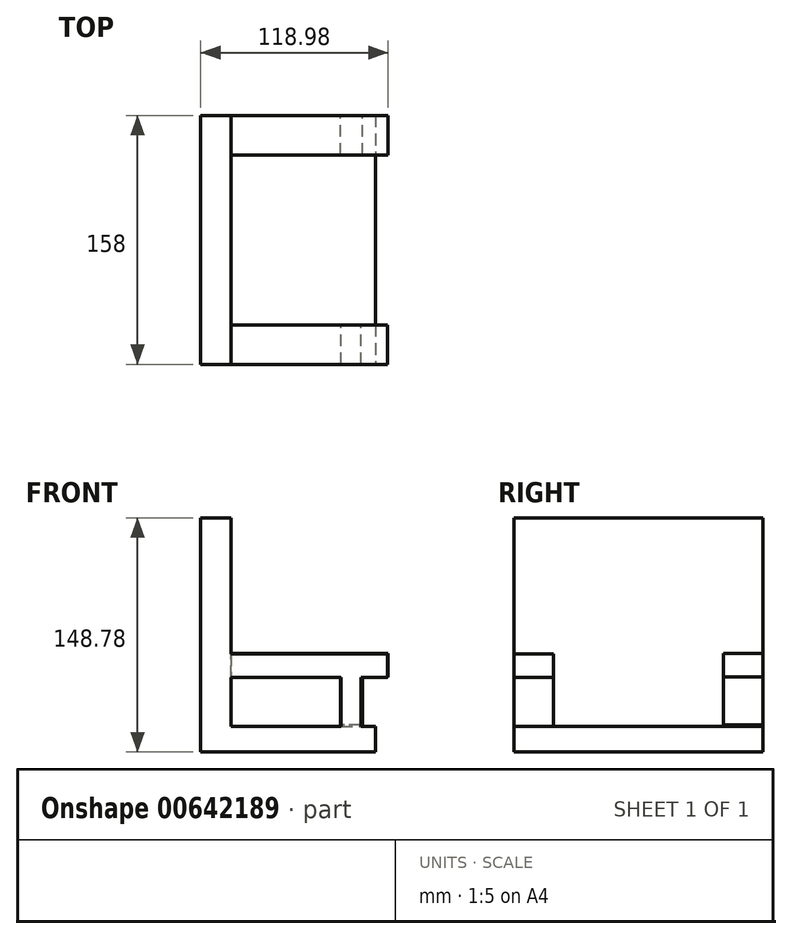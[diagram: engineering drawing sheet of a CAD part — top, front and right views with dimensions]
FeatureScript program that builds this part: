
annotation { "Feature Type Name" : "Feature", "Feature Type Description" : "" }
export const myFeature = defineFeature(function(context is Context, id is Id, definition is map)
    precondition{}
    {
        {
            var Q0;
            Q0=qCreatedBy(makeId("Front.planeOp"),FACE);
            var sketch = newSketch(context, id + "F0", { "sketchPlane" : qUnion([Q0])});
            skLineSegment(sketch, "E0.bottom", {"start": v(-39.67, -10.55) * mm, "end": v(51.82, -10.55) * mm});
            skLineSegment(sketch, "E0.top", {"start": v(-59.06, -26.93) * mm, "end": v(51.82, -26.93) * mm});
            skLineSegment(sketch, "E0.left", {"start": v(-59.06, -10.55) * mm, "end": v(-59.06, -26.93) * mm});
            skLineSegment(sketch, "E0.right", {"start": v(51.82, -10.55) * mm, "end": v(51.82, -26.93) * mm});
            skLineSegment(sketch, "E1.top", {"start": v(-59.06, 121.85) * mm, "end": v(-39.67, 121.85) * mm});
            skLineSegment(sketch, "E1.left", {"start": v(-59.06, -10.55) * mm, "end": v(-59.06, 121.85) * mm});
            skLineSegment(sketch, "E1.right", {"start": v(-39.67, -10.55) * mm, "end": v(-39.67, 121.85) * mm});
            skLineSegment(sketch, "E2.bottom", {"start": v(-39.67, 35.3) * mm, "end": v(59.63, 35.3) * mm});
            skLineSegment(sketch, "E2.top", {"start": v(-39.67, 20.45) * mm, "end": v(59.63, 20.45) * mm});
            skLineSegment(sketch, "E2.left", {"start": v(-39.67, 35.3) * mm, "end": v(-39.67, 20.45) * mm});
            skLineSegment(sketch, "E2.right", {"start": v(59.63, 35.3) * mm, "end": v(59.63, 20.45) * mm});
            skLineSegment(sketch, "E3.bottom", {"start": v(29.92, 20.45) * mm, "end": v(42.74, 20.45) * mm});
            skLineSegment(sketch, "E3.top", {"start": v(29.92, -10.55) * mm, "end": v(42.74, -10.55) * mm});
            skLineSegment(sketch, "E3.left", {"start": v(29.92, 20.45) * mm, "end": v(29.92, -10.55) * mm});
            skLineSegment(sketch, "E3.right", {"start": v(42.74, 20.45) * mm, "end": v(42.74, -10.55) * mm});
            skSolve(sketch);
        }
        {
            var Q0;
            Q0=makeQuery(id+"F0.imprint","IMPRINT",FACE,{"disambiguationData":[TD([[makeQuery(id+"F0.imprint","IMPRINT",EDGE,{"derivedFrom":sQuery(id+"F0.wireOp",EDGE,"E0.bottom")}),-1.0]])]});
            extrude(context, id + "F1", {"entities" : qUnion([Q0]), "oppositeDirection" : true, "depth" : 133 * mm, "offsetDistance" : 25 * mm});
        }
        {
            var Q0;
            Q0 = qSketchRegion(id + "F0", true);
            extrude(context, id + "F2", {"entities" : qUnion([Q0]), "operationType" : NewBodyOperationType.ADD, "depth" : 25 * mm, "offsetDistance" : 25 * mm});
        }
        {
            var Q0;
            Q0=qCreatedBy(makeId("Front.planeOp"),FACE);
            cPlane(context, id + "F3", {"entities" : qUnion([Q0]), "cplaneType" : CPlaneType.OFFSET, "offset" : 133 * mm, "oppositeDirection" : true, "width" : 150 * mm, "height" : 150 * mm});
        }
        {
            var Q0;
            Q0=qCreatedBy(id+"F3.planeOp",FACE);
            var sketch = newSketch(context, id + "F4", { "sketchPlane" : qUnion([Q0])});
            skLineSegment(sketch, "E4.bottom", {"start": v(59.92, 35.82) * mm, "end": v(-42.08, 35.82) * mm});
            skLineSegment(sketch, "E4.top", {"start": v(59.92, 20.8) * mm, "end": v(-42.08, 20.8) * mm});
            skLineSegment(sketch, "E4.left", {"start": v(59.92, 35.82) * mm, "end": v(59.92, 20.8) * mm});
            skLineSegment(sketch, "E4.right", {"start": v(-42.08, 35.82) * mm, "end": v(-42.08, 20.8) * mm});
            skLineSegment(sketch, "E5.bottom", {"start": v(43.65, 20.8) * mm, "end": v(29.88, 20.8) * mm});
            skLineSegment(sketch, "E5.top", {"start": v(43.65, -9.86) * mm, "end": v(29.88, -9.86) * mm});
            skLineSegment(sketch, "E5.left", {"start": v(43.65, 20.8) * mm, "end": v(43.65, -9.86) * mm});
            skLineSegment(sketch, "E5.right", {"start": v(29.88, 20.8) * mm, "end": v(29.88, -9.86) * mm});
            skSolve(sketch);
        }
        {
            var Q0;
            Q0 = qSketchRegion(id + "F4", true);
            extrude(context, id + "F5", {"entities" : qUnion([Q0]), "operationType" : NewBodyOperationType.ADD, "depth" : 25 * mm, "offsetDistance" : 25 * mm});
        }
    });
